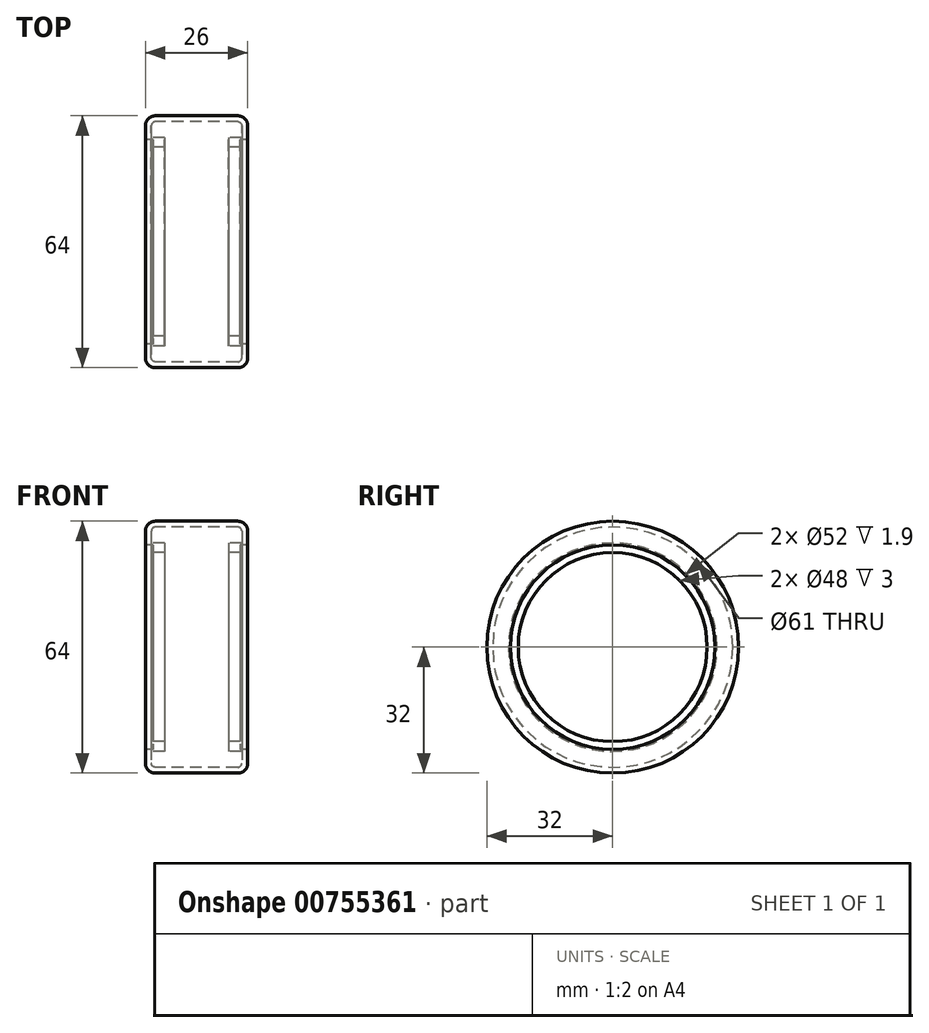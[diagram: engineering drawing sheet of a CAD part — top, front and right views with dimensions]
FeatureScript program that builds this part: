
annotation { "Feature Type Name" : "Feature", "Feature Type Description" : "" }
export const myFeature = defineFeature(function(context is Context, id is Id, definition is map)
    precondition{}
    {
        {
            var Q0;
            Q0=qCreatedBy(makeId("Front.planeOp"),FACE);
            var sketch = newSketch(context, id + "F0", { "sketchPlane" : qUnion([Q0])});
            skLineSegment(sketch, "E0", {"start": v(0, 0) * mm, "end": v(40.88, 0) * mm, "construction": true});
            skLineSegment(sketch, "E1", {"start": v(-10.5, 32) * mm, "end": v(10.5, 32) * mm});
            skLineSegment(sketch, "E2", {"start": v(0, 0) * mm, "end": v(0, 32) * mm, "construction": true});
            skLineSegment(sketch, "E3", {"start": v(13, 29.5) * mm, "end": v(13, 26) * mm});
            skLineSegment(sketch, "E4", {"start": v(13, 26) * mm, "end": v(11.1, 26) * mm});
            skLineSegment(sketch, "E5", {"start": v(11.1, 24) * mm, "end": v(11.1, 26) * mm});
            skLineSegment(sketch, "E6", {"start": v(11.1, 24) * mm, "end": v(8.1, 24) * mm});
            skLineSegment(sketch, "E7", {"start": v(8.1, 24) * mm, "end": v(8.1, 26.5) * mm});
            skPoint(sketch, "E8.visualSharp", {"position": v(13, 32) * mm});
            skArc(sketch, "E8.filletArc", {"start": v(13, 29.5) * mm, "mid": v(12.27, 31.27) * mm, "end": v(10.5, 32) * mm});
            skArc(sketch, "E9.MirrorCS", {"start": v(-13, 29.5) * mm, "mid": v(-12.27, 31.27) * mm, "end": v(-10.5, 32) * mm});
            skLineSegment(sketch, "E10.MirrorCS", {"start": v(-13, 29.5) * mm, "end": v(-13, 26) * mm});
            skLineSegment(sketch, "E11.MirrorCS", {"start": v(-13, 26) * mm, "end": v(-11.1, 26) * mm});
            skLineSegment(sketch, "E12.MirrorCS", {"start": v(-11.1, 24) * mm, "end": v(-11.1, 26) * mm});
            skLineSegment(sketch, "E13.MirrorCS", {"start": v(-11.1, 24) * mm, "end": v(-8.1, 24) * mm});
            skLineSegment(sketch, "E14.MirrorCS", {"start": v(-8.1, 24) * mm, "end": v(-8.1, 26.5) * mm});
            skPoint(sketch, "E15.orphan", {"position": v(-13, 32) * mm});
            skArc(sketch, "E16.0", {"start": v(11.5, 29.5) * mm, "mid": v(11.2, 30.2) * mm, "end": v(10.5, 30.5) * mm});
            skLineSegment(sketch, "E17.0", {"start": v(-10.5, 30.5) * mm, "end": v(10.5, 30.5) * mm});
            skLineSegment(sketch, "E18.0", {"start": v(11.5, 29.5) * mm, "end": v(11.5, 26.5) * mm});
            skLineSegment(sketch, "E19", {"start": v(8.1, 26.5) * mm, "end": v(11.5, 26.5) * mm});
            skArc(sketch, "E20.MirrorCS", {"start": v(-11.5, 29.5) * mm, "mid": v(-11.2, 30.2) * mm, "end": v(-10.5, 30.5) * mm});
            skLineSegment(sketch, "E21.MirrorCS", {"start": v(-11.5, 29.5) * mm, "end": v(-11.5, 26.5) * mm});
            skLineSegment(sketch, "E22.MirrorCS", {"start": v(-8.1, 26.5) * mm, "end": v(-11.5, 26.5) * mm});
            skSolve(sketch);
        }
        {
            var Q0;
            Q0=makeQuery(id+"F0.imprint","IMPRINT",FACE,{"disambiguationData":[TD([[makeQuery(id+"F0.imprint","IMPRINT",EDGE,{"derivedFrom":sQuery(id+"F0.wireOp",EDGE,"E1")}),-1.0]])]});
            var Q1;
            Q1=sQuery(id+"F0.wireOp",EDGE,"E0");
            revolve(context, id + "F1", {"surfaceOperationType" : NewSurfaceOperationType.NEW, "entities" : qUnion([Q0]), "axis" : qUnion([Q1]), "revolveType" : RevolveType.FULL});
        }
    });
